# Revit family: Sink-Undermount-Lavatory-KOHLER-Tahoe-K-2890-1
name_source: partatom
category: Plumbing Fixtures
revit_build: Autodesk Revit 2017 (Build: 20160225_1515(x64)
units: mm (PartAtom-declared; Revit-internal decimal feet)

## family parameters
Cut with Voids When Loaded = No
Host = Face
OmniClass Number = 23.31.13.00
Part Type = Normal
Room Calculation Point = No
Round Connector Dimension = Use Diameter
Shared = No

## types (4) — shared parameters
ADA Compliant = Yes
Assembly Code = D2010400
CW Connection = No
Cold Water Inlet = Cold Water Inlet
Date Modified = 08/13/2021
Default Elevation = 36"
Drain Included = No
HW Connection = No
Height = 8 9/16"
Hot Water Inlet = Hot Water Inlet
Length = 18"
Manufacturer = KOHLER Co.
Master Format 2014 = 22 41 16
Master Format 2014 Name = Residential Lavatories and Sinks
Material = Enameled Cast Iron
Product Documentation Link = https://www.us.kohler.com
Product Name = Tahoe
Product Page URL = http://www.us.kohler.com
URL = http://www.us.kohler.com
Vent Connection = No
Waste Connection = Yes
Waste Water Outlet = Waste Water Outlet
WaterSense Certified = No
Width = 20"

## per-type parameters (varying)
| type | 4" Faucet Hole Spacing | 8" Faucet Hole Spacing | Description | Faucet Hole Spacing | Finish | Model | Type |
| 4" Faucet Hole Spacing, 0-White | Yes | No | Undermount bathroom sink with 4 Inch oversize centerset faucet holes | 4" | KOHLER-Enameled_Cast_Iron-0-White | K-2890-4U-0 | 1 |
| 4" Faucet Hole Spacing, 96-Biscuit | Yes | No | Undermount bathroom sink with 4 Inch oversize centerset faucet holes | 4" | KOHLER-Enameled_Cast_Iron-96-Biscuit | K-2890-4U-96 | 2 |
| 8" Faucet Hole Spacing, 0-White | No | Yes | Undermount bathroom sink with 8 Inch oversize centerset faucet holes | 8" | KOHLER-Enameled_Cast_Iron-0-White | K-2890-8U-0 | 3 |
| 8" Faucet Hole Spacing, 96-Biscuit | No | Yes | Undermount bathroom sink with 8 Inch oversize centerset faucet holes | 8" | KOHLER-Enameled_Cast_Iron-96-Biscuit | K-2890-8U-96 | 4 |

## geometry (parser evidence)
native form markers: Sweep x5
no freeform markers — native parametric forms only
